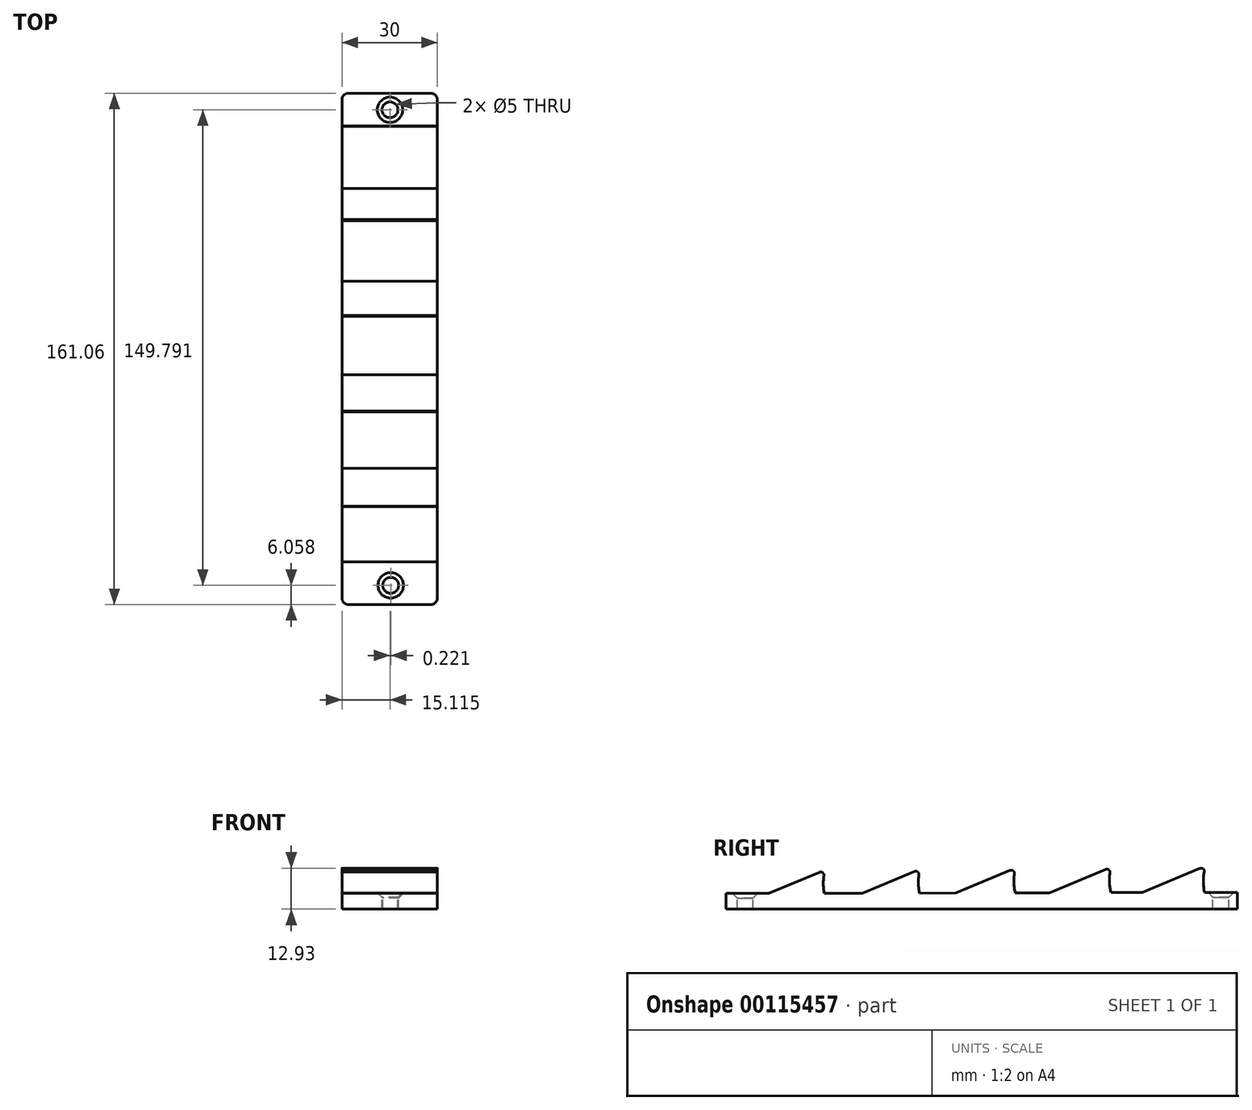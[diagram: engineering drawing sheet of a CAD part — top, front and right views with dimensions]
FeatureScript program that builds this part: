
annotation { "Feature Type Name" : "Feature", "Feature Type Description" : "" }
export const myFeature = defineFeature(function(context is Context, id is Id, definition is map)
    precondition{}
    {
        {
            var Q0;
            Q0=qCreatedBy(makeId("Right.planeOp"),FACE);
            var sketch = newSketch(context, id + "F0", { "sketchPlane" : qUnion([Q0])});
            skLineSegment(sketch, "E0", {"start": v(-103.28, 1.64) * mm, "end": v(36.72, 1.64) * mm});
            skLineSegment(sketch, "E1", {"start": v(-100.86, 6.61) * mm, "end": v(-83.13, 14.02) * mm});
            skArc(sketch, "E2", {"start": v(-83.13, 14.02) * mm, "mid": v(-83.67, 10.33) * mm, "end": v(-83.34, 6.61) * mm});
            skLineSegment(sketch, "E3", {"start": v(-71.4, 6.64) * mm, "end": v(-53.2, 14.24) * mm});
            skArc(sketch, "E4", {"start": v(-53.2, 14.24) * mm, "mid": v(-53.75, 10.48) * mm, "end": v(-53.39, 6.7) * mm});
            skLineSegment(sketch, "E5", {"start": v(-41.93, 6.72) * mm, "end": v(-23.12, 14.58) * mm});
            skArc(sketch, "E6", {"start": v(-23.12, 14.58) * mm, "mid": v(-23.66, 10.68) * mm, "end": v(-23.24, 6.77) * mm});
            skLineSegment(sketch, "E7", {"start": v(-12.46, 6.8) * mm, "end": v(6.97, 14.92) * mm});
            skArc(sketch, "E8", {"start": v(6.97, 14.92) * mm, "mid": v(6.43, 10.9) * mm, "end": v(6.92, 6.86) * mm});
            skLineSegment(sketch, "E9", {"start": v(16.72, 6.88) * mm, "end": v(36.78, 15.26) * mm});
            skArc(sketch, "E10", {"start": v(36.78, 15.26) * mm, "mid": v(36.03, 11.1) * mm, "end": v(36.39, 6.88) * mm});
            skLineSegment(sketch, "E11", {"start": v(36.72, 1.64) * mm, "end": v(46.72, 1.64) * mm});
            skLineSegment(sketch, "E12", {"start": v(46.72, 1.64) * mm, "end": v(46.72, 5.64) * mm});
            skLineSegment(sketch, "E13", {"start": v(6.92, 6.86) * mm, "end": v(16.72, 6.88) * mm});
            skLineSegment(sketch, "E14", {"start": v(16.72, 6.88) * mm, "end": v(6.92, 6.86) * mm});
            skPoint(sketch, "E15.orphan", {"position": v(-13.08, 6.54) * mm});
            skPoint(sketch, "E16.orphan", {"position": v(-23.18, 6.52) * mm});
            skLineSegment(sketch, "E17.trimOffspring", {"start": v(-12.46, 6.8) * mm, "end": v(-23.24, 6.77) * mm});
            skLineSegment(sketch, "E18.trimOffspring", {"start": v(-41.93, 6.72) * mm, "end": v(-53.39, 6.7) * mm});
            skPoint(sketch, "E19.orphan", {"position": v(-53.27, 6.18) * mm});
            skPoint(sketch, "E20.orphan", {"position": v(-43.18, 6.2) * mm});
            skLineSegment(sketch, "E21.trimOffspring", {"start": v(-71.4, 6.64) * mm, "end": v(-83.34, 6.61) * mm});
            skPoint(sketch, "E22.orphan", {"position": v(-73.27, 5.86) * mm});
            skPoint(sketch, "E23.orphan", {"position": v(-83.2, 5.95) * mm});
            skLineSegment(sketch, "E24", {"start": v(36.39, 6.88) * mm, "end": v(46.72, 6.88) * mm});
            skPoint(sketch, "E25.orphan", {"position": v(36.72, 5.64) * mm});
            skLineSegment(sketch, "E26", {"start": v(46.72, 5.64) * mm, "end": v(46.72, 6.88) * mm});
            skLineSegment(sketch, "E27.top", {"start": v(-103.2, 1.64) * mm, "end": v(-103.28, 1.64) * mm});
            skLineSegment(sketch, "E28", {"start": v(-100.86, 6.61) * mm, "end": v(-114.34, 6.61) * mm});
            skLineSegment(sketch, "E29", {"start": v(-114.34, 6.61) * mm, "end": v(-114.34, 1.64) * mm});
            skPoint(sketch, "E27.right.end.orphan", {"position": v(-110.77, 1.64) * mm});
            skPoint(sketch, "E30.orphan", {"position": v(-103.2, 5.64) * mm});
            skLineSegment(sketch, "E31", {"start": v(-103.2, 1.64) * mm, "end": v(-114.34, 1.64) * mm});
            skSolve(sketch);
        }
        {
            var Q0;
            Q0=qSketchRegion(id+"F0",true);
            var Q1;
            Q1=sQuery(id+"F0.wireOp",EDGE,"E0");
            var Q2;
            Q2=sQuery(id+"F0.wireOp",EDGE,"E1");
            var Q3;
            Q3=sQuery(id+"F0.wireOp",EDGE,"E2");
            var Q4;
            Q4=sQuery(id+"F0.wireOp",EDGE,"aVXR79yY-1hjt-y3u3-m6eV-zaEhtOIxPnFv");
            var Q5;
            Q5=sQuery(id+"F0.wireOp",EDGE,"4554b6e0-54a2-462e-aa4e-58822ef9da20");
            var Q6;
            Q6=sQuery(id+"F0.wireOp",EDGE,"E3");
            var Q7;
            Q7=sQuery(id+"F0.wireOp",EDGE,"E4");
            var Q8;
            Q8=sQuery(id+"F0.wireOp",EDGE,"a5485bb7-b8e9-40f3-8546-a96ed6ddff3a");
            var Q9;
            Q9=sQuery(id+"F0.wireOp",EDGE,"E5");
            var Q10;
            Q10=sQuery(id+"F0.wireOp",EDGE,"E6");
            var Q11;
            Q11=sQuery(id+"F0.wireOp",EDGE,"a28d2f95-e289-46cd-9a1f-94b747a0afc5");
            var Q12;
            Q12=sQuery(id+"F0.wireOp",EDGE,"E7");
            var Q13;
            Q13=sQuery(id+"F0.wireOp",EDGE,"E8");
            var Q14;
            Q14=sQuery(id+"F0.wireOp",EDGE,"E12");
            var Q15;
            Q15=sQuery(id+"F0.wireOp",EDGE,"ae9abd8c-4da3-48e8-ab53-a4a2666a44f8");
            var Q16;
            Q16=sQuery(id+"F0.wireOp",EDGE,"E11");
            var Q17;
            Q17=sQuery(id+"F0.wireOp",EDGE,"E9");
            var Q18;
            Q18=sQuery(id+"F0.wireOp",EDGE,"E10");
            var Q19;
            Q19=sQuery(id+"F0.wireOp",EDGE,"KTlvuNxW-LSAw-ywOI-KxQU-ba1FE6igpGGa");
            extrude(context, id + "F1", {"entities" : qUnion([Q0]), "surfaceEntities" : qUnion([Q1, Q2, Q3, Q4, Q5, Q6, Q7, Q8, Q9, Q10, Q11, Q12, Q13, Q14, Q15, Q16, Q17, Q18, Q19]), "depth" : 30 * mm});
        }
        {
            var Q0;
            Q0=makeQuery(id+"F1.opExtrude","CAP_EDGE",EDGE,{"disambiguationData":[OSD([sQuery(id+"F0.wireOp",EDGE,"E29")])],"isStart":true});
            var Q1;
            Q1=makeQuery(id+"F1.opExtrude","CAP_EDGE",EDGE,{"disambiguationData":[OSD([sQuery(id+"F0.wireOp",EDGE,"E29")])],"isStart":false});
            var Q2;
            Q2=makeQuery(id+"F1.opExtrude","CAP_EDGE",EDGE,{"disambiguationData":[OSD([sQuery(id+"F0.wireOp",EDGE,"E12"),sQuery(id+"F0.wireOp",EDGE,"E26")])],"isStart":true});
            var Q3;
            Q3=makeQuery(id+"F1.opExtrude","CAP_EDGE",EDGE,{"disambiguationData":[OSD([sQuery(id+"F0.wireOp",EDGE,"E12"),sQuery(id+"F0.wireOp",EDGE,"E26")])],"isStart":false});
            fillet(context, id + "F2", {"entities" : qUnion([Q0, Q1, Q2, Q3]), "radius" : 2 * mm, "tangentPropagation" : true, "allowEdgeOverflow" : false});
        }
        {
            var Q0;
            Q0=makeQuery(id+"F1.opExtrude","SWEPT_EDGE",EDGE,{"disambiguationData":[OSD([sQuery(id+"F0.wireOp",EDGE,"E9"),sQuery(id+"F0.wireOp",EDGE,"E10")])]});
            var Q1;
            Q1=makeQuery(id+"F1.opExtrude","SWEPT_EDGE",EDGE,{"disambiguationData":[OSD([sQuery(id+"F0.wireOp",EDGE,"E7"),sQuery(id+"F0.wireOp",EDGE,"E8")])]});
            var Q2;
            Q2=makeQuery(id+"F1.opExtrude","SWEPT_EDGE",EDGE,{"disambiguationData":[OSD([sQuery(id+"F0.wireOp",EDGE,"E5"),sQuery(id+"F0.wireOp",EDGE,"E6")])]});
            var Q3;
            Q3=makeQuery(id+"F1.opExtrude","SWEPT_EDGE",EDGE,{"disambiguationData":[OSD([sQuery(id+"F0.wireOp",EDGE,"E3"),sQuery(id+"F0.wireOp",EDGE,"E4")])]});
            var Q4;
            Q4=makeQuery(id+"F1.opExtrude","SWEPT_EDGE",EDGE,{"disambiguationData":[OSD([sQuery(id+"F0.wireOp",EDGE,"E1"),sQuery(id+"F0.wireOp",EDGE,"E2")])]});
            fillet(context, id + "F3", {"entities" : qUnion([Q0, Q1, Q2, Q3, Q4]), "radius" : 1 * mm, "tangentPropagation" : true, "allowEdgeOverflow" : false});
        }
        {
            var Q0;
            Q0=makeQuery(id+"F1.opExtrude","SWEPT_FACE",FACE,{"disambiguationData":[OSD([sQuery(id+"F0.wireOp",EDGE,"E28")])]});
            var sketch = newSketch(context, id + "F4", { "sketchPlane" : qUnion([Q0])});
            skPoint(sketch, "E32", {"position": v(15.34, -108.28) * mm});
            skPoint(sketch, "E33", {"position": v(161.37, -142.1) * mm});
            skSolve(sketch);
        }
        {
            var Q0;
            Q0=sQuery(id+"F4.wireOp",VERTEX,"E32");
            var Q1;
            Q1=makeQuery(id+"F1.opExtrude","SWEPT_BODY",BODY,{"disambiguationData":[OSD([sQuery(id+"F0.wireOp",EDGE,"E0"),sQuery(id+"F0.wireOp",EDGE,"E1"),sQuery(id+"F0.wireOp",EDGE,"E2"),sQuery(id+"F0.wireOp",EDGE,"E3"),sQuery(id+"F0.wireOp",EDGE,"E4"),sQuery(id+"F0.wireOp",EDGE,"E5"),sQuery(id+"F0.wireOp",EDGE,"E6"),sQuery(id+"F0.wireOp",EDGE,"E7"),sQuery(id+"F0.wireOp",EDGE,"E8"),sQuery(id+"F0.wireOp",EDGE,"E9"),sQuery(id+"F0.wireOp",EDGE,"E10"),sQuery(id+"F0.wireOp",EDGE,"E11"),sQuery(id+"F0.wireOp",EDGE,"E12"),sQuery(id+"F0.wireOp",EDGE,"E14"),sQuery(id+"F0.wireOp",EDGE,"E17.trimOffspring"),sQuery(id+"F0.wireOp",EDGE,"E18.trimOffspring"),sQuery(id+"F0.wireOp",EDGE,"E21.trimOffspring"),sQuery(id+"F0.wireOp",EDGE,"E24"),sQuery(id+"F0.wireOp",EDGE,"E26"),sQuery(id+"F0.wireOp",EDGE,"E28"),sQuery(id+"F0.wireOp",EDGE,"E29"),sQuery(id+"F0.wireOp",EDGE,"E31")])]});
            hole(context, id + "F5", {"style" : HoleStyle.C_SINK, "holeDiameter" : 5 * mm, "cSinkDiameter" : 8 * mm, "endStyle" : HoleEndStyle.THROUGH, "locations" : qUnion([Q0]), "scope" : qUnion([Q1]), "cSinkAngle" : 90 * degree});
        }
        {
            var Q0;
            Q0=makeQuery(id+"F1.opExtrude","SWEPT_FACE",FACE,{"disambiguationData":[OSD([sQuery(id+"F0.wireOp",EDGE,"E24")])]});
            var sketch = newSketch(context, id + "F6", { "sketchPlane" : qUnion([Q0])});
            skPoint(sketch, "E34", {"position": v(15.11, 41.5) * mm});
            skSolve(sketch);
        }
        {
            var Q0;
            Q0=sQuery(id+"F6.wireOp",VERTEX,"E34");
            var Q1;
            Q1=makeQuery(id+"F1.opExtrude","SWEPT_BODY",BODY,{"disambiguationData":[OSD([sQuery(id+"F0.wireOp",EDGE,"E0"),sQuery(id+"F0.wireOp",EDGE,"E1"),sQuery(id+"F0.wireOp",EDGE,"E2"),sQuery(id+"F0.wireOp",EDGE,"E3"),sQuery(id+"F0.wireOp",EDGE,"E4"),sQuery(id+"F0.wireOp",EDGE,"E5"),sQuery(id+"F0.wireOp",EDGE,"E6"),sQuery(id+"F0.wireOp",EDGE,"E7"),sQuery(id+"F0.wireOp",EDGE,"E8"),sQuery(id+"F0.wireOp",EDGE,"E9"),sQuery(id+"F0.wireOp",EDGE,"E10"),sQuery(id+"F0.wireOp",EDGE,"E11"),sQuery(id+"F0.wireOp",EDGE,"E12"),sQuery(id+"F0.wireOp",EDGE,"E14"),sQuery(id+"F0.wireOp",EDGE,"E17.trimOffspring"),sQuery(id+"F0.wireOp",EDGE,"E18.trimOffspring"),sQuery(id+"F0.wireOp",EDGE,"E21.trimOffspring"),sQuery(id+"F0.wireOp",EDGE,"E24"),sQuery(id+"F0.wireOp",EDGE,"E26"),sQuery(id+"F0.wireOp",EDGE,"E28"),sQuery(id+"F0.wireOp",EDGE,"E29"),sQuery(id+"F0.wireOp",EDGE,"E31")])]});
            hole(context, id + "F7", {"style" : HoleStyle.C_SINK, "holeDiameter" : 5 * mm, "cSinkDiameter" : 8 * mm, "endStyle" : HoleEndStyle.THROUGH, "locations" : qUnion([Q0]), "scope" : qUnion([Q1]), "cSinkAngle" : 90 * degree});
        }
    });
